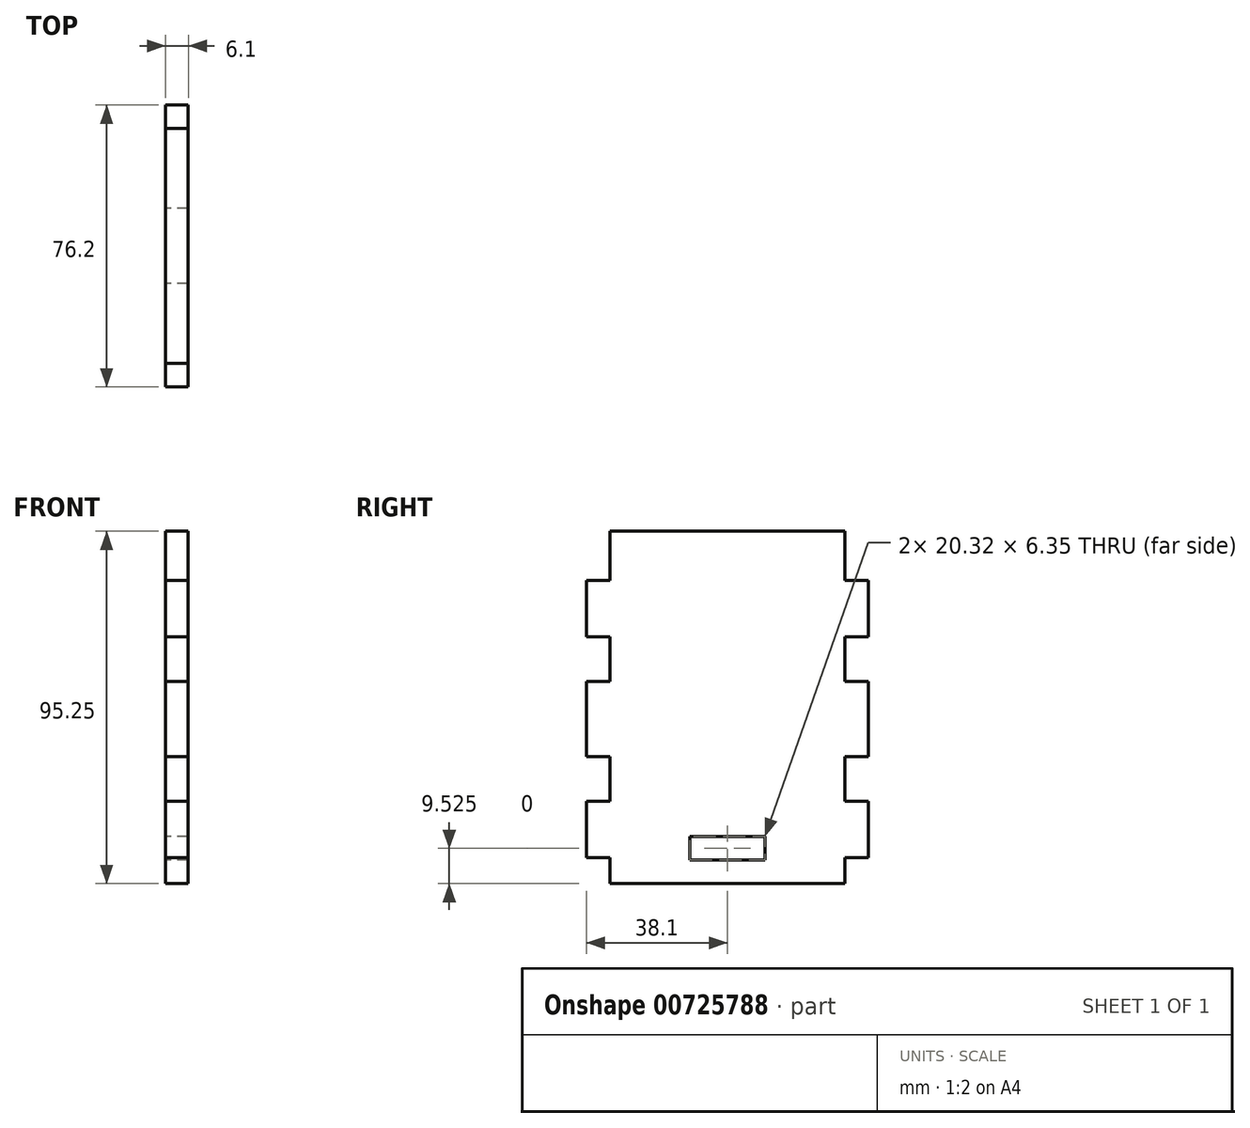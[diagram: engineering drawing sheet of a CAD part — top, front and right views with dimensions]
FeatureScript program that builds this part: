
annotation { "Feature Type Name" : "Feature", "Feature Type Description" : "" }
export const myFeature = defineFeature(function(context is Context, id is Id, definition is map)
    precondition{}
    {
        {
            var Q0;
            Q0=qCreatedBy(makeId("Right.planeOp"),FACE);
            var sketch = newSketch(context, id + "F0", { "sketchPlane" : qUnion([Q0])});
            skLineSegment(sketch, "E0.bottom", {"start": v(0, 0) * mm, "end": v(63.5, 0) * mm});
            skLineSegment(sketch, "E0.left", {"start": v(0, 0) * mm, "end": v(0, 6.98) * mm});
            skLineSegment(sketch, "E0.right", {"start": v(63.5, 0) * mm, "end": v(63.5, 6.99) * mm});
            skLineSegment(sketch, "E1.right", {"start": v(21.6, 6.35) * mm, "end": v(21.6, 12.7) * mm});
            skLineSegment(sketch, "E2.MirrorCS", {"start": v(41.9, 6.35) * mm, "end": v(41.9, 12.7) * mm});
            skLineSegment(sketch, "E3.top", {"start": v(0, 54.61) * mm, "end": v(-6.35, 54.61) * mm});
            skLineSegment(sketch, "E3.right", {"start": v(-6.35, 44.45) * mm, "end": v(-6.35, 54.61) * mm});
            skLineSegment(sketch, "E4.MirrorCS", {"start": v(0, 34.3) * mm, "end": v(-6.35, 34.3) * mm});
            skLineSegment(sketch, "E5.MirrorCS", {"start": v(-6.35, 44.45) * mm, "end": v(-6.35, 34.3) * mm});
            skLineSegment(sketch, "E6.bottom", {"start": v(0, 66.68) * mm, "end": v(-6.35, 66.68) * mm});
            skLineSegment(sketch, "E6.top", {"start": v(0, 81.92) * mm, "end": v(-6.35, 81.92) * mm});
            skLineSegment(sketch, "E6.right", {"start": v(-6.35, 66.68) * mm, "end": v(-6.35, 81.92) * mm});
            skLineSegment(sketch, "E7.MirrorCS", {"start": v(0, 22.22) * mm, "end": v(-6.35, 22.22) * mm});
            skLineSegment(sketch, "E8.MirrorCS", {"start": v(-6.35, 22.22) * mm, "end": v(-6.35, 6.98) * mm});
            skLineSegment(sketch, "E9.MirrorCS", {"start": v(0, 6.98) * mm, "end": v(-6.35, 6.98) * mm});
            skLineSegment(sketch, "E10.trimOffspring", {"start": v(0, 54.61) * mm, "end": v(0, 66.68) * mm});
            skPoint(sketch, "E3.left.start.orphan", {"position": v(0, 44.45) * mm});
            skLineSegment(sketch, "E11.trimOffspring", {"start": v(0, 22.22) * mm, "end": v(0, 34.3) * mm});
            skLineSegment(sketch, "E12.MirrorCS", {"start": v(63.5, 54.61) * mm, "end": v(69.85, 54.61) * mm});
            skLineSegment(sketch, "E13.MirrorCS", {"start": v(69.85, 44.45) * mm, "end": v(69.85, 54.61) * mm});
            skLineSegment(sketch, "E14.MirrorCS", {"start": v(69.85, 44.45) * mm, "end": v(69.85, 34.3) * mm});
            skLineSegment(sketch, "E15.MirrorCS", {"start": v(63.5, 34.3) * mm, "end": v(69.85, 34.3) * mm});
            skLineSegment(sketch, "E16.MirrorCS", {"start": v(69.85, 66.68) * mm, "end": v(69.85, 81.92) * mm});
            skLineSegment(sketch, "E17.MirrorCS", {"start": v(63.5, 81.92) * mm, "end": v(69.85, 81.92) * mm});
            skLineSegment(sketch, "E18.MirrorCS", {"start": v(63.5, 66.68) * mm, "end": v(69.85, 66.68) * mm});
            skLineSegment(sketch, "E19.MirrorCS", {"start": v(63.5, 22.23) * mm, "end": v(69.85, 22.23) * mm});
            skLineSegment(sketch, "E20.MirrorCS", {"start": v(69.85, 22.23) * mm, "end": v(69.85, 6.99) * mm});
            skLineSegment(sketch, "E21.MirrorCS", {"start": v(63.5, 6.99) * mm, "end": v(69.85, 6.99) * mm});
            skPoint(sketch, "E22.orphan", {"position": v(31.75, 88.9) * mm});
            skPoint(sketch, "E23.start.orphan", {"position": v(31.75, 0) * mm});
            skLineSegment(sketch, "E24.trimOffspring", {"start": v(63.5, 22.23) * mm, "end": v(63.5, 34.3) * mm});
            skLineSegment(sketch, "E25.trimOffspring", {"start": v(63.5, 54.61) * mm, "end": v(63.5, 66.68) * mm});
            skLineSegment(sketch, "E26", {"start": v(0, 95.25) * mm, "end": v(63.5, 95.25) * mm});
            skLineSegment(sketch, "E27", {"start": v(0, 95.25) * mm, "end": v(0, 81.92) * mm});
            skLineSegment(sketch, "E28", {"start": v(63.5, 81.92) * mm, "end": v(63.5, 95.25) * mm});
            skLineSegment(sketch, "E29", {"start": v(21.6, 12.7) * mm, "end": v(41.9, 12.7) * mm});
            skLineSegment(sketch, "E30", {"start": v(41.9, 6.35) * mm, "end": v(21.6, 6.35) * mm});
            skSolve(sketch);
        }
        {
            var Q0;
            Q0=makeQuery(id+"F0.imprint","IMPRINT",FACE,{"disambiguationData":[TD([[makeQuery(id+"F0.imprint","IMPRINT",EDGE,{"derivedFrom":sQuery(id+"F0.wireOp",EDGE,"E0.bottom")}),1.0]])]});
            extrude(context, id + "F1", {"entities" : qUnion([Q0]), "depth" : 6.1 * mm, "offsetDistance" : 25.4 * mm});
        }
    });
